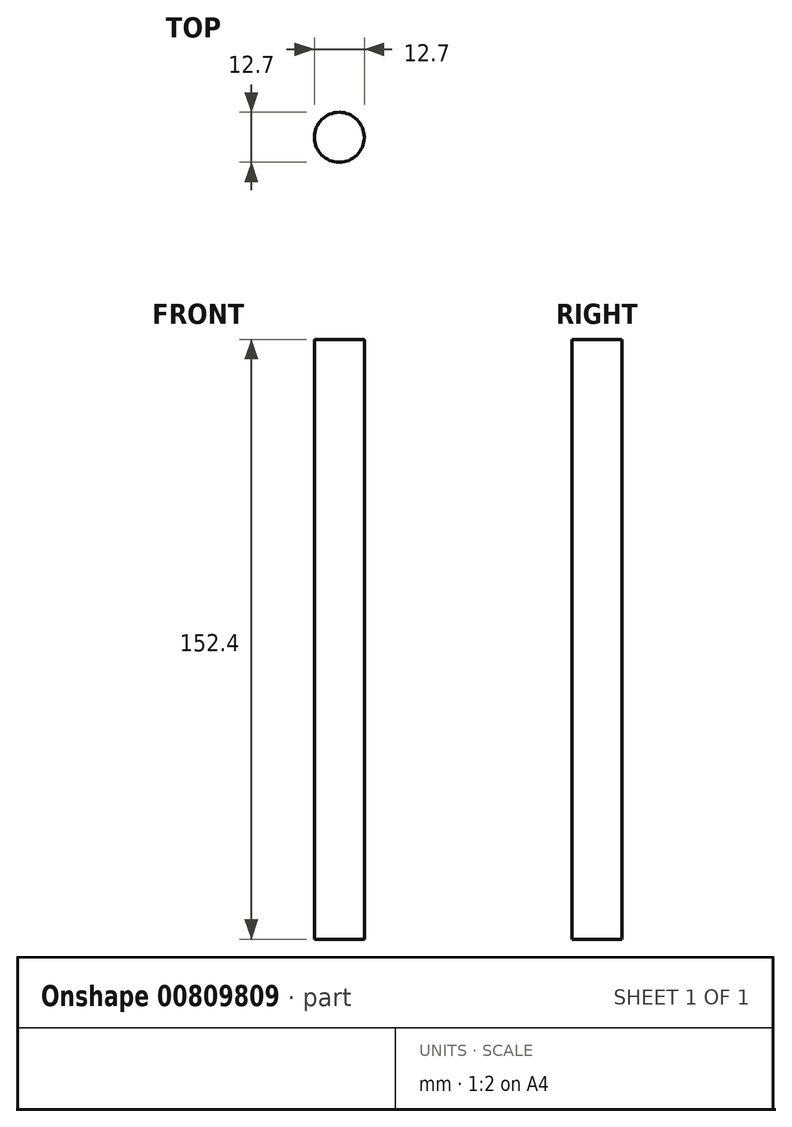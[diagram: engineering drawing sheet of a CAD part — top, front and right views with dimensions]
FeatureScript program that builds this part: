
annotation { "Feature Type Name" : "Feature", "Feature Type Description" : "" }
export const myFeature = defineFeature(function(context is Context, id is Id, definition is map)
    precondition{}
    {
        {
            var Q0;
            Q0=qCreatedBy(makeId("Top.planeOp"),FACE);
            var sketch = newSketch(context, id + "F0", { "sketchPlane" : qUnion([Q0])});
            skCircle(sketch, "E0", {"center": v(0, -7.42) * mm, "radius": 6.35 * mm});
            skSolve(sketch);
        }
        {
            var Q0;
            Q0=qSketchRegion(id+"F0",true);
            extrude(context, id + "F1", {"entities" : qUnion([Q0]), "depth" : 152.4 * mm, "offsetDistance" : 25.4 * mm});
        }
    });
